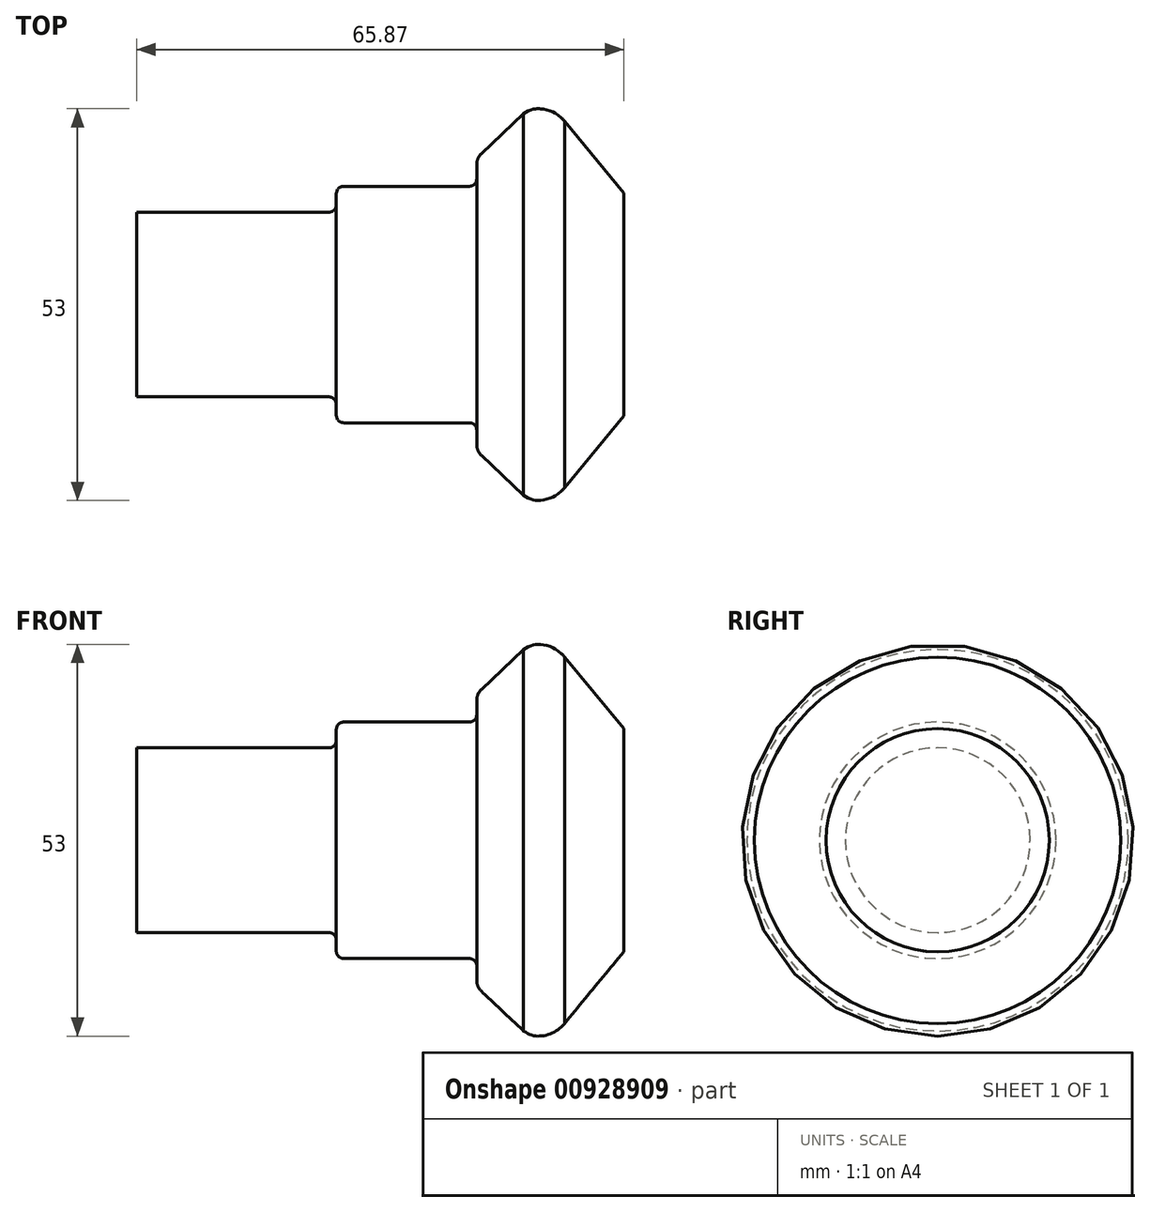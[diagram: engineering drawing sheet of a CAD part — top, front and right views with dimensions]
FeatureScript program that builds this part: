
annotation { "Feature Type Name" : "Feature", "Feature Type Description" : "" }
export const myFeature = defineFeature(function(context is Context, id is Id, definition is map)
    precondition{}
    {
        {
            var Q0;
            Q0=qCreatedBy(makeId("Front.planeOp"),FACE);
            var sketch = newSketch(context, id + "F0", { "sketchPlane" : qUnion([Q0])});
            skLineSegment(sketch, "E0", {"start": v(-8, 24.79) * mm, "end": v(0, 15.1) * mm});
            skFitSpline(sketch, "E1", {"points": [v(-14.03, 25.48) * mm, v(-12.46, 26.36) * mm, v(-10.97, 26.46) * mm, v(-9.36, 25.94) * mm, v(-8.23, 25.07) * mm, v(-8, 24.79) * mm], "startDerivative": vector(6.57, 4.44) * mm, "endDerivative": vector(1.73, -2.25) * mm});
            skLineSegment(sketch, "E2", {"start": v(-19.87, 0) * mm, "end": v(-26.87, 0) * mm});
            skLineSegment(sketch, "E3", {"start": v(-19.87, 0) * mm, "end": v(0, 0) * mm});
            skLineSegment(sketch, "E4", {"start": v(0, 15.1) * mm, "end": v(0, 0) * mm});
            skLineSegment(sketch, "E5", {"start": v(-19.24, 20.43) * mm, "end": v(-13.51, 25.83) * mm});
            skPoint(sketch, "E6.visualSharp", {"position": v(-19.87, 19.84) * mm});
            skArc(sketch, "E6.filletArc", {"start": v(-19.24, 20.43) * mm, "mid": v(-19.7, 19.77) * mm, "end": v(-19.87, 18.97) * mm});
            skLineSegment(sketch, "E7", {"start": v(-20.87, 16) * mm, "end": v(-37.87, 16) * mm});
            skLineSegment(sketch, "E8", {"start": v(-38.87, 15) * mm, "end": v(-38.87, 13.5) * mm});
            skLineSegment(sketch, "E9", {"start": v(-39.87, 12.5) * mm, "end": v(-65.87, 12.5) * mm});
            skLineSegment(sketch, "E10", {"start": v(-65.87, 12.5) * mm, "end": v(-65.87, 0) * mm});
            skLineSegment(sketch, "E11", {"start": v(-19.87, 17) * mm, "end": v(-19.87, 18.97) * mm});
            skPoint(sketch, "E12.visualSharp", {"position": v(-38.87, 12.5) * mm});
            skArc(sketch, "E12.filletArc", {"start": v(-39.87, 12.5) * mm, "mid": v(-39.16, 12.8) * mm, "end": v(-38.87, 13.5) * mm});
            skPoint(sketch, "E13.visualSharp", {"position": v(-19.87, 16) * mm});
            skArc(sketch, "E13.filletArc", {"start": v(-20.87, 16) * mm, "mid": v(-20.16, 16.3) * mm, "end": v(-19.87, 17) * mm});
            skLineSegment(sketch, "E14", {"start": v(-26.87, 0) * mm, "end": v(-65.87, 0) * mm});
            skPoint(sketch, "E15.visualSharp", {"position": v(-38.87, 16) * mm});
            skArc(sketch, "E15.filletArc", {"start": v(-37.87, 16) * mm, "mid": v(-38.57, 15.7) * mm, "end": v(-38.87, 15) * mm});
            skSolve(sketch);
        }
        {
            var Q0;
            Q0=makeQuery(id+"F0.imprint","IMPRINT",FACE,{"disambiguationData":[TD([[makeQuery(id+"F0.imprint","IMPRINT",EDGE,{"derivedFrom":sQuery(id+"F0.wireOp",EDGE,"E0")}),-1.0]])]});
            var Q1;
            Q1=sQuery(id+"F0.wireOp",EDGE,"E14");
            revolve(context, id + "F1", {"surfaceOperationType" : NewSurfaceOperationType.NEW, "entities" : qUnion([Q0]), "axis" : qUnion([Q1]), "revolveType" : RevolveType.FULL});
        }
    });
